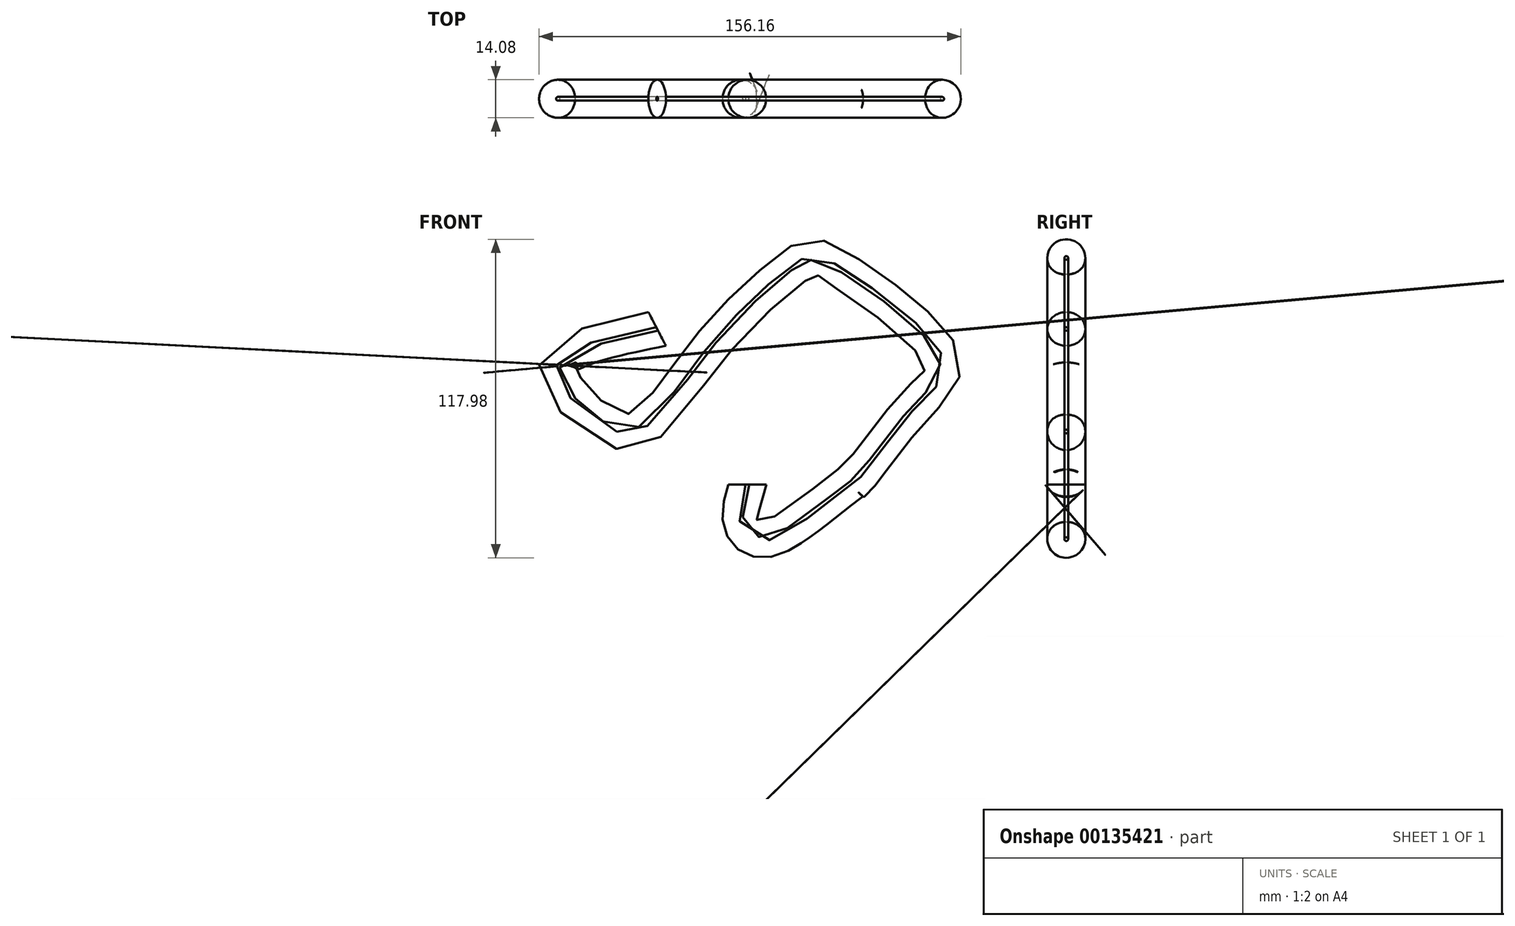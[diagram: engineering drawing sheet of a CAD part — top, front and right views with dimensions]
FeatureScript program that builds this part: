
annotation { "Feature Type Name" : "Feature", "Feature Type Description" : "" }
export const myFeature = defineFeature(function(context is Context, id is Id, definition is map)
    precondition{}
    {
        {
            var Q0;
            Q0=qCreatedBy(makeId("Front.planeOp"),FACE);
            var sketch = newSketch(context, id + "F0", { "sketchPlane" : qUnion([Q0])});
            skFitSpline(sketch, "E0.0", {"points": [v(-28, 24.8) * mm, v(-30.68, 24.26) * mm, v(-36, 23.17) * mm, v(-43.6, 21.46) * mm, v(-50.52, 19.6) * mm, v(-55.44, 17.89) * mm, v(-58.7, 16.43) * mm, v(-60.75, 15.31) * mm, v(-62.35, 14.21) * mm, v(-63.5, 13.18) * mm, v(-64.2, 12.3) * mm, v(-64.5, 11.7) * mm, v(-64.65, 11.25) * mm, v(-64.7, 10.96) * mm, v(-64.73, 10.7) * mm, v(-64.75, 10.43) * mm, v(-64.74, 10) * mm, v(-64.66, 9.36) * mm, v(-64.45, 8.37) * mm, v(-63.96, 6.88) * mm, v(-63, 4.84) * mm, v(-61.23, 1.92) * mm, v(-58.25, -1.9) * mm, v(-53.79, -6.21) * mm, v(-49.7, -9.2) * mm, v(-46.46, -11.02) * mm, v(-44.11, -12.06) * mm, v(-42.3, -12.65) * mm, v(-40.98, -12.94) * mm, v(-40.06, -13.07) * mm, v(-39.23, -13.13) * mm, v(-38.44, -13.1) * mm, v(-37.67, -13.03) * mm, v(-36.65, -12.83) * mm, v(-35.36, -12.43) * mm, v(-33.72, -11.64) * mm, v(-32, -10.52) * mm, v(-29.56, -8.58) * mm, v(-26.36, -5.35) * mm, v(-22.34, -0.42) * mm, v(-18.85, 4.3) * mm, v(-15.94, 8.3) * mm, v(-13.7, 11.37) * mm, v(-11.74, 13.96) * mm, v(-10.14, 16.03) * mm, v(-8.9, 17.6) * mm, v(-7.65, 19.13) * mm, v(-5.96, 21.16) * mm, v(-3.81, 23.63) * mm, v(-1.2, 26.49) * mm, v(2.27, 30.16) * mm, v(6.58, 34.43) * mm, v(10.7, 38.23) * mm, v(13.77, 40.95) * mm, v(15.96, 42.82) * mm, v(18, 44.5) * mm, v(19.56, 45.75) * mm, v(20.72, 46.64) * mm, v(21.55, 47.27) * mm, v(22.33, 47.84) * mm, v(22.93, 48.28) * mm, v(23.4, 48.6) * mm, v(23.73, 48.84) * mm, v(24, 49.02) * mm, v(24.22, 49.16) * mm, v(24.43, 49.3) * mm, v(24.7, 49.47) * mm, v(25.18, 49.77) * mm, v(25.9, 50.17) * mm, v(27.02, 50.66) * mm, v(28.46, 51.05) * mm, v(30.05, 51.17) * mm, v(31.54, 51) * mm, v(32.79, 50.67) * mm, v(33.83, 50.28) * mm, v(34.76, 49.85) * mm, v(35.96, 49.24) * mm, v(37.6, 48.32) * mm, v(39.88, 46.95) * mm, v(42.43, 45.33) * mm, v(45.22, 43.5) * mm, v(48.19, 41.48) * mm, v(51.27, 39.3) * mm, v(54.43, 37.01) * mm, v(57.59, 34.63) * mm, v(60.7, 32.2) * mm, v(63.7, 29.74) * mm, v(66.54, 27.3) * mm, v(69.18, 24.87) * mm, v(71.55, 22.5) * mm, v(73.28, 20.53) * mm, v(74.51, 18.95) * mm, v(75.35, 17.72) * mm, v(75.99, 16.64) * mm, v(76.44, 15.71) * mm, v(76.85, 14.75) * mm, v(77.27, 13.46) * mm, v(77.54, 11.77) * mm, v(77.53, 10.02) * mm, v(77.22, 8.33) * mm, v(76.67, 6.8) * mm, v(75.98, 5.51) * mm, v(75.23, 4.41) * mm, v(74.2, 3.15) * mm, v(72.93, 1.84) * mm, v(71.67, 0.64) * mm, v(70.64, -0.32) * mm, v(70, -0.95) * mm, v(69.48, -1.46) * mm, v(69.09, -1.85) * mm, v(68.69, -2.27) * mm, v(68.14, -2.85) * mm, v(67.43, -3.62) * mm, v(66.24, -4.95) * mm, v(64.06, -7.48) * mm, v(60.76, -11.54) * mm, v(57.47, -15.79) * mm, v(54.95, -19.09) * mm, v(53.16, -21.45) * mm, v(51.49, -23.66) * mm, v(49.96, -25.67) * mm, v(48.82, -27.14) * mm, v(48, -28.17) * mm, v(47.42, -28.87) * mm, v(46.88, -29.52) * mm, v(46.35, -30.11) * mm, v(45.78, -30.7) * mm, v(45.12, -31.3) * mm, v(44.5, -31.75) * mm, v(44.06, -32.03) * mm, v(43.7, -32.24) * mm, v(43.4, -32.4) * mm, v(43.25, -32.49) * mm, v(43.15, -32.55) * mm, v(43.06, -32.6) * mm, v(42.94, -32.68) * mm, v(42.8, -32.77) * mm, v(42.6, -32.91) * mm, v(42.27, -33.15) * mm, v(41.55, -33.7) * mm, v(40.18, -34.76) * mm, v(38.16, -36.37) * mm, v(35.85, -38.21) * mm, v(33.32, -40.22) * mm, v(30.66, -42.3) * mm, v(27.92, -44.38) * mm, v(25.17, -46.4) * mm, v(22.46, -48.27) * mm, v(20.27, -49.67) * mm, v(18.56, -50.65) * mm, v(17.29, -51.33) * mm, v(16, -51.92) * mm, v(14.66, -52.44) * mm, v(13.43, -52.79) * mm, v(12.3, -52.98) * mm, v(11.34, -53.05) * mm, v(10.25, -53.01) * mm, v(9.07, -52.8) * mm, v(7.86, -52.4) * mm, v(6.68, -51.76) * mm, v(5.64, -50.93) * mm, v(4.8, -49.98) * mm, v(4.16, -49) * mm, v(3.71, -48.06) * mm, v(3.41, -47.17) * mm, v(3.15, -46.06) * mm, v(3.01, -44.82) * mm, v(3.01, -43.49) * mm, v(3.1, -42.24) * mm, v(3.27, -41.03) * mm, v(3.56, -39.45) * mm, v(4.01, -37.48) * mm, v(4.65, -35.11) * mm, v(5.1, -33.55) * mm, v(5.3, -32.79) * mm]});
            skSolve(sketch);
        }
        {
            var Q0;
            Q0=qCreatedBy(makeId("Top.planeOp"),FACE);
            var Q1;
            Q1=sQuery(id+"F0.wireOp",VERTEX,"E0.0.end");
            cPlane(context, id + "F1", {"entities" : qUnion([Q0, Q1]), "cplaneType" : CPlaneType.PLANE_POINT, "offset" : 25.4 * mm, "width" : 152.4 * mm, "height" : 152.4 * mm});
        }
        {
            var Q0;
            Q0=qCreatedBy(id+"F1.planeOp",FACE);
            var sketch = newSketch(context, id + "F2", { "sketchPlane" : qUnion([Q0])});
            skCircle(sketch, "E1", {"center": v(5.33, 0) * mm, "radius": 0.7 * mm});
            skCircle(sketch, "E2.0", {"center": v(5.33, 0) * mm, "radius": 7.04 * mm});
            skSolve(sketch);
        }
        {
            var Q0;
            Q0=makeQuery(id+"F2.imprint","IMPRINT",FACE,{"disambiguationData":[TD([[makeQuery(id+"F2.imprint","IMPRINT",EDGE,{"derivedFrom":sQuery(id+"F2.wireOp",EDGE,"E1")}),-1.0]])]});
            var Q1;
            Q1=sQuery(id+"F2.wireOp",EDGE,"E1");
            var Q2;
            Q2=sQuery(id+"F0.wireOp",EDGE,"E0.0");
            sweep(context, id + "F3", {"profiles" : qUnion([Q0]), "surfaceProfiles" : qUnion([Q1]), "path" : qUnion([Q2])});
        }
    });
